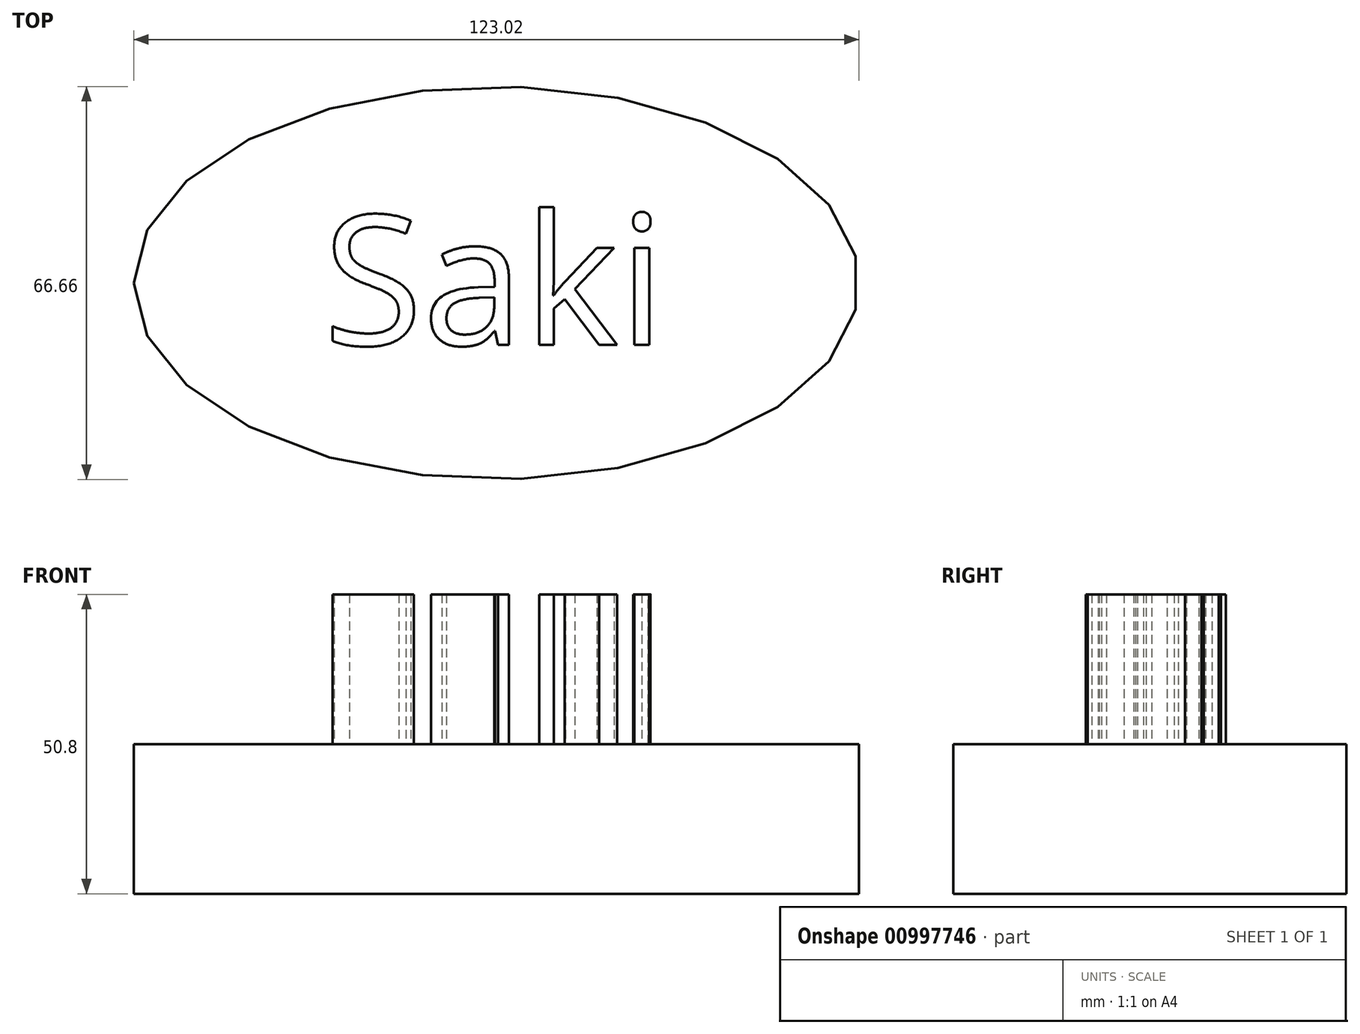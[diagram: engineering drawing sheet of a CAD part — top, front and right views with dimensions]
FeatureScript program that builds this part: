
annotation { "Feature Type Name" : "Feature", "Feature Type Description" : "" }
export const myFeature = defineFeature(function(context is Context, id is Id, definition is map)
    precondition{}
    {
        {
            var Q0;
            Q0=qCreatedBy(makeId("Top.planeOp"),FACE);
            var sketch = newSketch(context, id + "F0", { "sketchPlane" : qUnion([Q0])});
            skEllipse(sketch, "E0", {"center": v(0, 0) * mm, "majorRadius": 61.51 * mm, "minorRadius": 33.33 * mm, "majorAxis": v(-1, 0)});
            skSolve(sketch);
        }
        {
            var Q0;
            Q0 = qSketchRegion(id + "F0", true);
            extrude(context, id + "F1", {"entities" : qUnion([Q0]), "depth" : 25.4 * mm, "offsetDistance" : 25.4 * mm});
        }
        {
            var Q0;
            Q0=makeQuery(id+"F1.opExtrude","CAP_FACE",FACE,{"disambiguationData":[OSD([sQuery(id+"F0.wireOp",EDGE,"E0")])],"isStart":false});
            var sketch = newSketch(context, id + "F2", { "sketchPlane" : qUnion([Q0])});
            skText(sketch, "E1", { "text": "Saki", "fontName": "OpenSans-Regular.ttf"});
            const initialGuessF2  = {"E1": [-0.02938, -0.01052, 1, 0, 0.02216]};
            skSetInitialGuess(sketch, initialGuessF2);
            skSolve(sketch);
        }
        {
            var Q0;
            Q0 = qSketchRegion(id + "F2", true);
            extrude(context, id + "F3", {"entities" : qUnion([Q0]), "operationType" : NewBodyOperationType.ADD, "depth" : 25.4 * mm, "offsetDistance" : 25.4 * mm});
        }
    });
